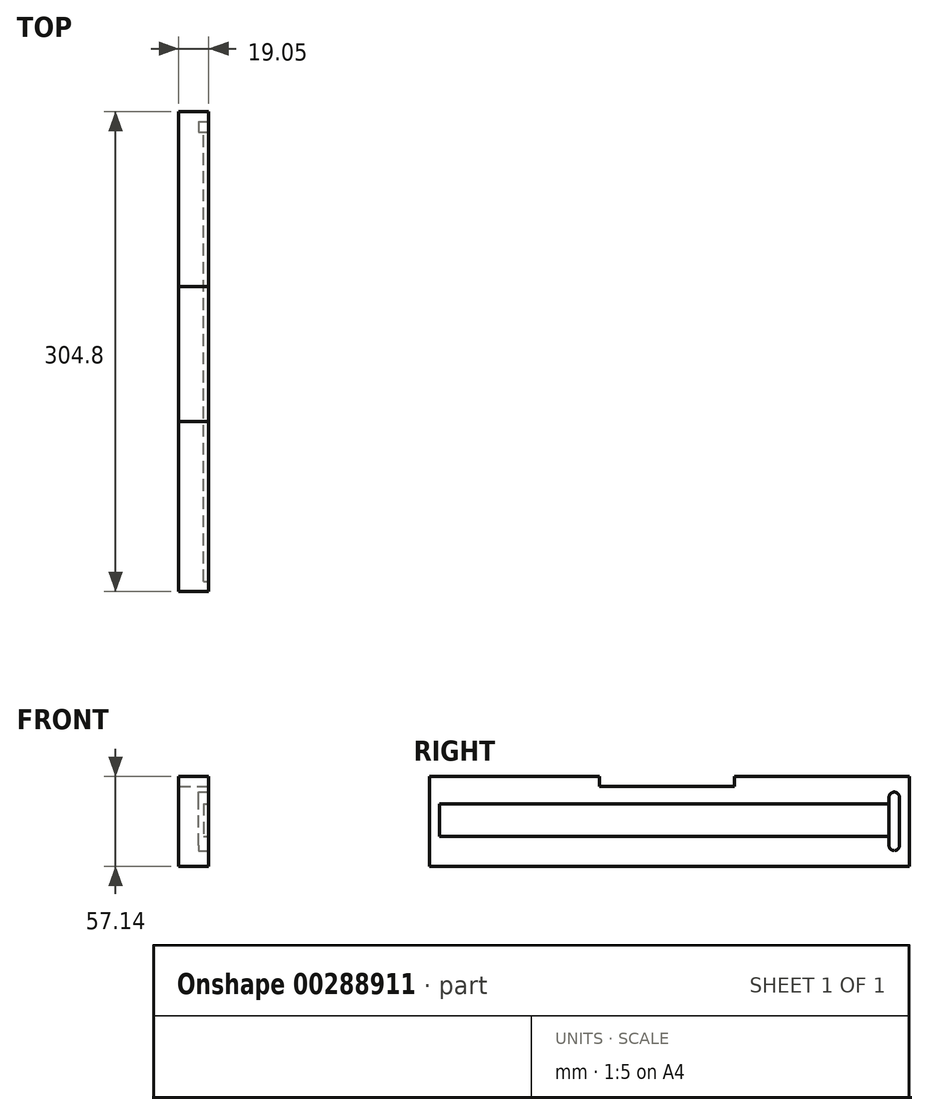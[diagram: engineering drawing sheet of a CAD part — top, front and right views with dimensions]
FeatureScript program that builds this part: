
annotation { "Feature Type Name" : "Feature", "Feature Type Description" : "" }
export const myFeature = defineFeature(function(context is Context, id is Id, definition is map)
    precondition{}
    {
        {
            var Q0;
            Q0=qCreatedBy(makeId("Right.planeOp"),FACE);
            var sketch = newSketch(context, id + "F0", { "sketchPlane" : qUnion([Q0])});
            skLineSegment(sketch, "E0.bottom", {"start": v(-152.4, 28.57) * mm, "end": v(152.4, 28.57) * mm});
            skLineSegment(sketch, "E0.top", {"start": v(-152.4, -28.57) * mm, "end": v(152.4, -28.57) * mm});
            skLineSegment(sketch, "E0.left", {"start": v(-152.4, 28.57) * mm, "end": v(-152.4, -28.57) * mm});
            skLineSegment(sketch, "E0.right", {"start": v(152.4, 28.57) * mm, "end": v(152.4, -28.57) * mm});
            skPoint(sketch, "E0.middle", {"position": v(0, 0) * mm});
            skSolve(sketch);
        }
        {
            var Q0;
            Q0 = qSketchRegion(id + "F0", true);
            extrude(context, id + "F1", {"entities" : qUnion([Q0]), "depth" : 19.05 * mm});
        }
        {
            var Q0;
            Q0=makeQuery(id+"F1.opExtrude","CAP_FACE",FACE,{"disambiguationData":[OSD([sQuery(id+"F0.wireOp",EDGE,"E0.bottom"),sQuery(id+"F0.wireOp",EDGE,"E0.top"),sQuery(id+"F0.wireOp",EDGE,"E0.left"),sQuery(id+"F0.wireOp",EDGE,"E0.right")])],"isStart":false});
            var sketch = newSketch(context, id + "F2", { "sketchPlane" : qUnion([Q0])});
            skLineSegment(sketch, "E1", {"start": v(152.4, 18.6) * mm, "end": v(-152.4, 18.6) * mm, "construction": true});
            skLineSegment(sketch, "E2", {"start": v(152.4, -18.58) * mm, "end": v(-152.4, -18.58) * mm, "construction": true});
            skLineSegment(sketch, "E3", {"start": v(142.88, 28.57) * mm, "end": v(142.88, -28.57) * mm, "construction": true});
            skLineSegment(sketch, "E4", {"start": v(139.34, 28.57) * mm, "end": v(139.34, -28.57) * mm, "construction": true});
            skLineSegment(sketch, "E5", {"start": v(146.05, 28.57) * mm, "end": v(146.05, -28.57) * mm, "construction": true});
            skLineSegment(sketch, "E6", {"start": v(-152.4, 15.24) * mm, "end": v(139.34, 15.24) * mm, "construction": true});
            skLineSegment(sketch, "E7", {"start": v(-152.4, -15.23) * mm, "end": v(139.34, -15.23) * mm, "construction": true});
            skLineSegment(sketch, "E8", {"start": v(139.34, 15.24) * mm, "end": v(139.34, -15.23) * mm});
            skLineSegment(sketch, "E9", {"start": v(142.7, -15.23) * mm, "end": v(142.88, -15.23) * mm});
            skLineSegment(sketch, "E10", {"start": v(146.05, -15.23) * mm, "end": v(146.05, 15.24) * mm});
            skLineSegment(sketch, "E11", {"start": v(142.88, 15.24) * mm, "end": v(142.7, 15.24) * mm});
            skArc(sketch, "E12", {"start": v(146.05, 15.24) * mm, "mid": v(142.7, 18.6) * mm, "end": v(139.34, 15.24) * mm});
            skArc(sketch, "E13", {"start": v(139.34, -15.23) * mm, "mid": v(142.7, -18.58) * mm, "end": v(146.05, -15.23) * mm});
            skLineSegment(sketch, "E14.trimOffspring", {"start": v(142.7, 15.24) * mm, "end": v(142.88, 15.24) * mm, "construction": true});
            skLineSegment(sketch, "E15.trimOffspring", {"start": v(146.05, 15.24) * mm, "end": v(152.4, 15.24) * mm, "construction": true});
            skLineSegment(sketch, "E16.trimOffspring", {"start": v(142.7, -15.23) * mm, "end": v(142.88, -15.23) * mm, "construction": true});
            skLineSegment(sketch, "E17.trimOffspring", {"start": v(146.05, -15.23) * mm, "end": v(152.4, -15.23) * mm, "construction": true});
            skSolve(sketch);
        }
        {
            var Q0;
            Q0 = qSketchRegion(id + "F2", true);
            extrude(context, id + "F3", {"entities" : qUnion([Q0]), "operationType" : NewBodyOperationType.REMOVE, "oppositeDirection" : true, "depth" : 6.35 * mm});
        }
        {
            var Q0;
            Q0=makeQuery(id+"F1.opExtrude","CAP_FACE",FACE,{"disambiguationData":[OSD([sQuery(id+"F0.wireOp",EDGE,"E0.bottom"),sQuery(id+"F0.wireOp",EDGE,"E0.top"),sQuery(id+"F0.wireOp",EDGE,"E0.left"),sQuery(id+"F0.wireOp",EDGE,"E0.right")])],"isStart":false});
            var sketch = newSketch(context, id + "F4", { "sketchPlane" : qUnion([Q0])});
            skLineSegment(sketch, "E18", {"start": v(152.4, 11.18) * mm, "end": v(-152.4, 11.18) * mm, "construction": true});
            skLineSegment(sketch, "E19", {"start": v(-146.05, 28.57) * mm, "end": v(-146.05, -28.57) * mm, "construction": true});
            skLineSegment(sketch, "E20.bottom", {"start": v(-146.05, 11.18) * mm, "end": v(139.34, 11.18) * mm});
            skLineSegment(sketch, "E20.top", {"start": v(-146.05, -9.52) * mm, "end": v(139.34, -9.52) * mm});
            skLineSegment(sketch, "E20.left", {"start": v(-146.05, 11.18) * mm, "end": v(-146.05, -9.52) * mm});
            skLineSegment(sketch, "E20.right", {"start": v(139.34, 11.18) * mm, "end": v(139.34, -9.52) * mm});
            skSolve(sketch);
        }
        {
            var Q0;
            Q0 = qSketchRegion(id + "F4", true);
            extrude(context, id + "F5", {"entities" : qUnion([Q0]), "operationType" : NewBodyOperationType.REMOVE, "oppositeDirection" : true, "depth" : 3.17 * mm});
        }
        {
            var Q0;
            Q0=makeQuery(id+"F1.opExtrude","CAP_FACE",FACE,{"disambiguationData":[OSD([sQuery(id+"F0.wireOp",EDGE,"E0.bottom"),sQuery(id+"F0.wireOp",EDGE,"E0.top"),sQuery(id+"F0.wireOp",EDGE,"E0.left"),sQuery(id+"F0.wireOp",EDGE,"E0.right")])],"isStart":false});
            var sketch = newSketch(context, id + "F6", { "sketchPlane" : qUnion([Q0])});
            skLineSegment(sketch, "E21.bottom", {"start": v(-44.45, 28.57) * mm, "end": v(41.27, 28.57) * mm});
            skLineSegment(sketch, "E21.top", {"start": v(-44.45, 22.22) * mm, "end": v(41.27, 22.22) * mm});
            skLineSegment(sketch, "E21.left", {"start": v(-44.45, 28.57) * mm, "end": v(-44.45, 22.22) * mm});
            skLineSegment(sketch, "E21.right", {"start": v(41.27, 28.57) * mm, "end": v(41.27, 22.22) * mm});
            skSolve(sketch);
        }
        {
            var Q0;
            Q0 = qSketchRegion(id + "F6", true);
            extrude(context, id + "F7", {"entities" : qUnion([Q0]), "operationType" : NewBodyOperationType.REMOVE, "endBound" : BoundingType.UP_TO_NEXT, "oppositeDirection" : true, "depth" : 25.4 * mm});
        }
    });
